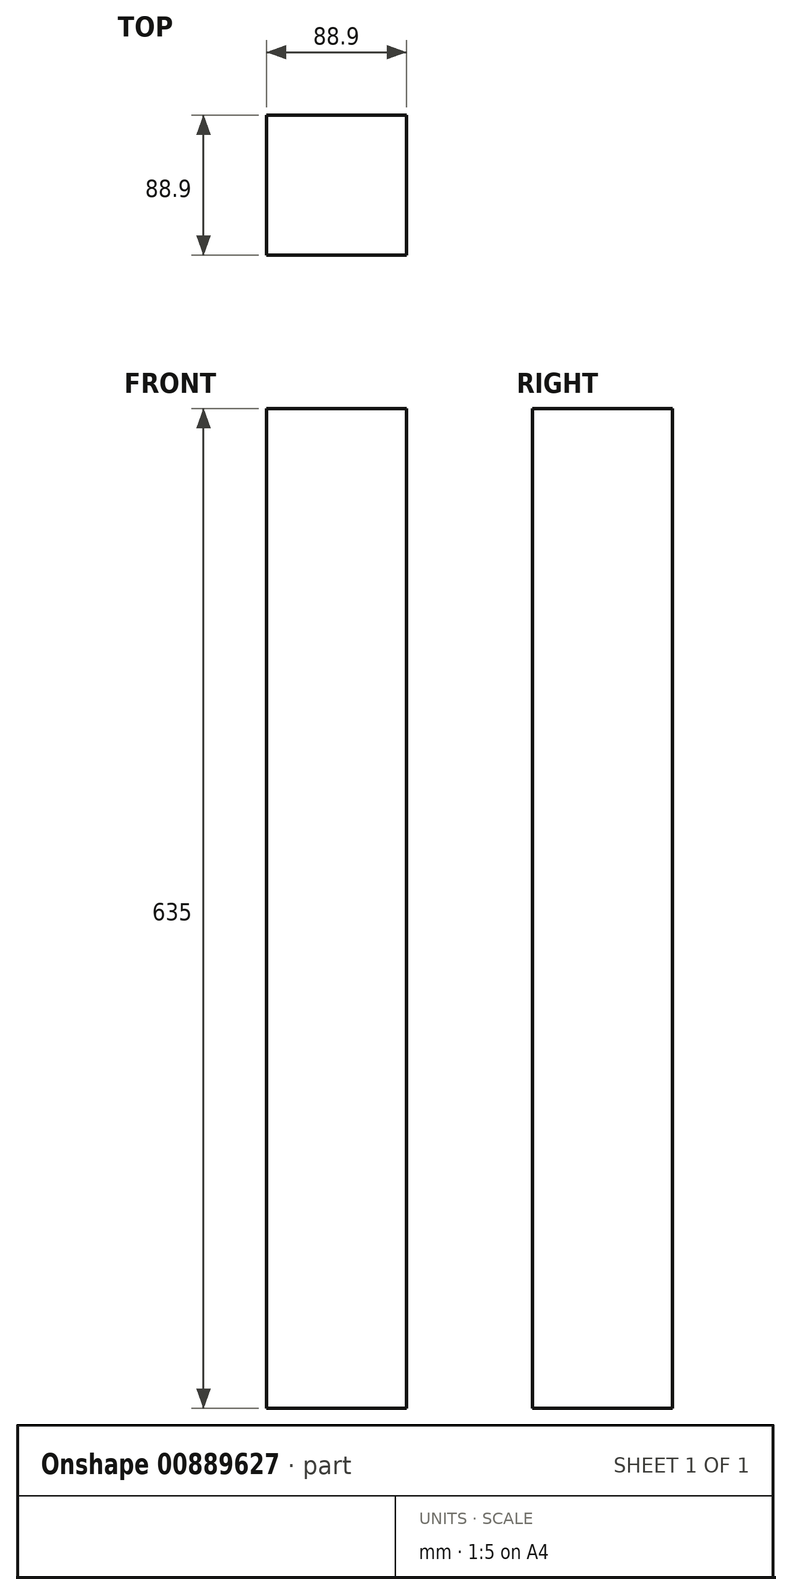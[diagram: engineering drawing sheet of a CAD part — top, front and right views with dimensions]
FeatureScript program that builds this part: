
annotation { "Feature Type Name" : "Feature", "Feature Type Description" : "" }
export const myFeature = defineFeature(function(context is Context, id is Id, definition is map)
    precondition{}
    {
        {
            var Q0;
            Q0=qCreatedBy(makeId("Top.planeOp"),FACE);
            var sketch = newSketch(context, id + "F0", { "sketchPlane" : qUnion([Q0])});
            skLineSegment(sketch, "E0.bottom", {"start": v(0, 0) * mm, "end": v(88.9, 0) * mm});
            skLineSegment(sketch, "E0.top", {"start": v(0, 88.9) * mm, "end": v(88.9, 88.9) * mm});
            skLineSegment(sketch, "E0.left", {"start": v(0, 0) * mm, "end": v(0, 88.9) * mm});
            skLineSegment(sketch, "E0.right", {"start": v(88.9, 0) * mm, "end": v(88.9, 88.9) * mm});
            skSolve(sketch);
        }
        {
            var Q0;
            Q0 = qSketchRegion(id + "F0", true);
            extrude(context, id + "F1", {"entities" : qUnion([Q0]), "depth" : 635 * mm, "offsetDistance" : 25.4 * mm});
        }
    });
